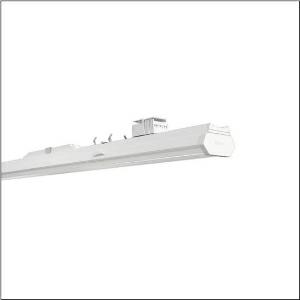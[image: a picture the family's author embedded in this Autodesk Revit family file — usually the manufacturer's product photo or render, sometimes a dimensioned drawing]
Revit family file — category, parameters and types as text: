
# Revit family: licross_r__21_protected_mo_52td12dnd75f_7536
name_source: partatom
category: Lighting Fixtures
units: mm (PartAtom-declared; Revit-internal decimal feet)

## family parameters
Cut with Voids When Loaded = No
Host = Face
Light Source = No
Part Type = Normal
Room Calculation Point = No
Round Connector Dimension = Use Diameter
Shared = No

## types (1)
- --- (1 x LED, 7710 lm, 61 W, 4000K)
    Apparent Load = 61 VA
    CIE Flux Codes = 73 92 98 99 100
    Color Rendering = 90
    Color Temperature = 4000K
    Default Elevation = 1800 mm
    Description = Licross® 21 Protected MOluminaire insert, length: 1.500mm, width: 90mm, height: 101mm, LED rated luminous flux: 7.710lm, light colour: 940, control gear: DALI 2, control gear: ECG DALI, with plug, 5-pole, with phase selection, mains connection: 220..240V, AC, 50/60Hz, halogen-free wiring, primary optical cover: cover, of PMMA, light emission: direct with ceiling illumination distribution, protection rating (complete): IP54, insulation class (complete): insulation class I (protective earthing), certification: CE, ENEC, VDE, UKCA, protection symbol: D if used in an environment with non-conductive dust loads with corresponding accessories, permissible ambient temperature for indoor applications: -25..+40°C, corresponds to IFS (International Featured Standards) requirements for safety and quality in the food industry, reducing of maximum allowable ambient temperature of 5°C with ceiling mounting, packaging unit: 1 piece
    Height = 92 mm
    Lamp = 1 x LED
    Lamp Light Flux = 7710 lm
    Lamp Power = 61 W
    Lamp count = 1
    Length = 1500 mm
    Luminous efficacy = 126 lm/W
    Manufacturer = Siteco
    ModVariant = No
    Model = 52TD12DND75F
    Mounting Place = Ceiling
    Mounting Type = Pendant
    Number of Poles = 1
    OnlyDefault = Yes
    Power Factor = 1
    Product Name = Licross® 21 Protected MO
    Product group = luminaire insert
    ProductGroupID = 902
    Protection Class = Protection class I
    Protection Degree = IP 54
    RLX_Detail_Level = 1
    RlxData = <blob elided: 24201 chars, md5=234d13ff>
    Socket = socket
    Standby Power = 0 W
    System Light Flux = 7710 lm
    System Power = 61 W
    Type Comments = factory setting: luminous flux: 100 % | dim-lin: 254 | 405 mA
    Type Image = l_1256148.jpg
    URL = http://relux.com
    VarID = @adj_129365
    Voltage = 0 V
    Weight = 0.00 kg
    Width = 88 mm

## geometry (parser evidence)
native form markers: Blend x4, Sweep x11
no freeform markers — native parametric forms only
